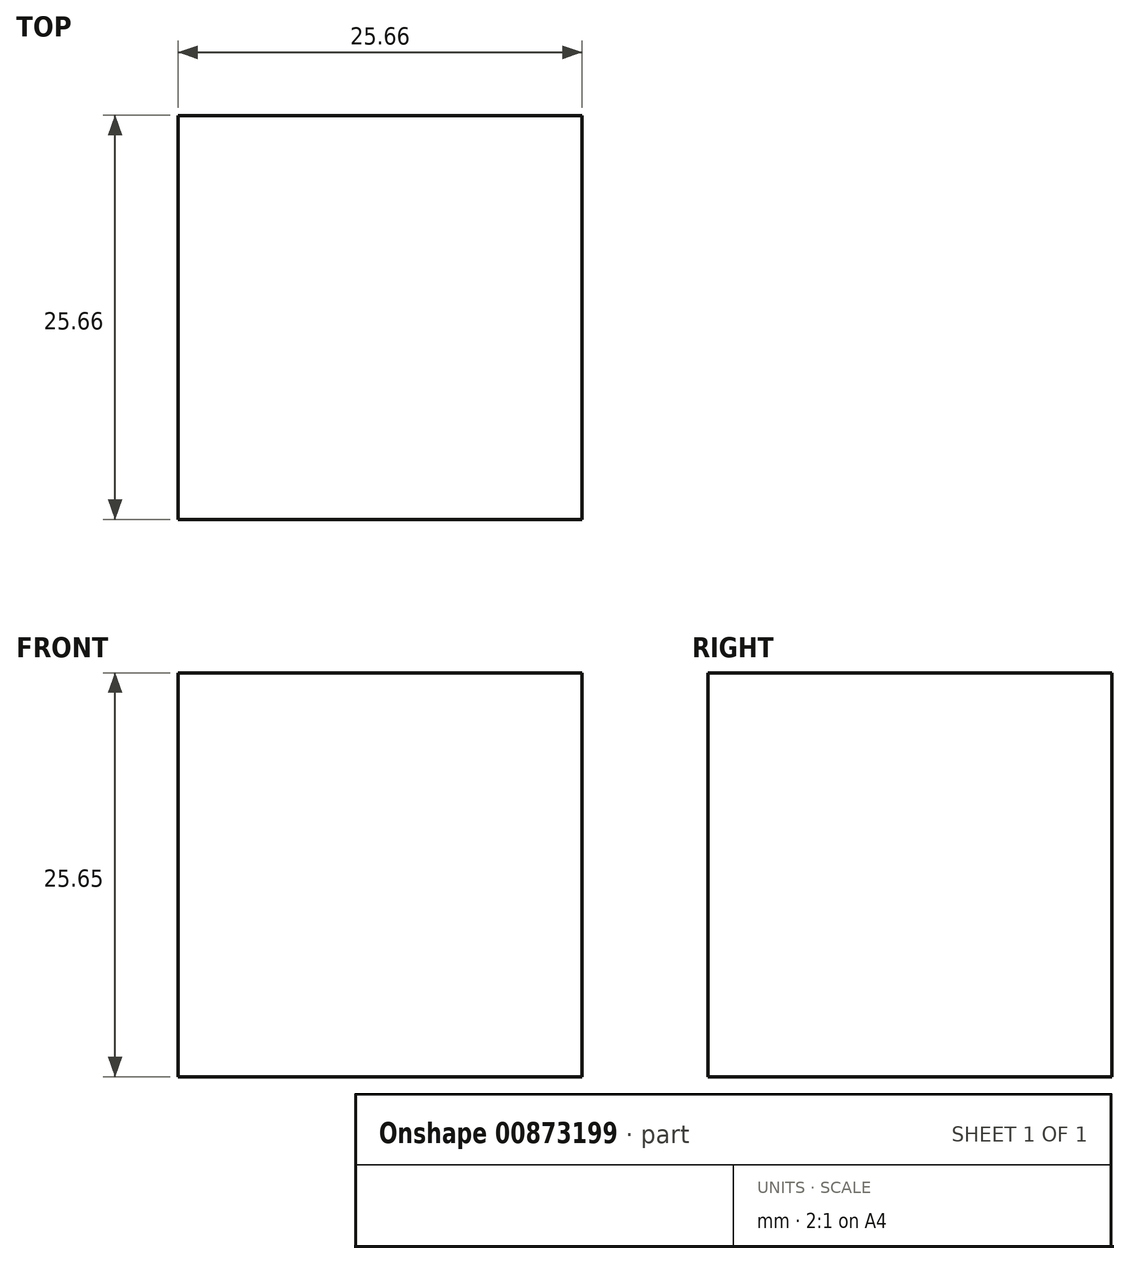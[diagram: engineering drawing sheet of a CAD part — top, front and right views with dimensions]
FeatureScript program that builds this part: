
annotation { "Feature Type Name" : "Feature", "Feature Type Description" : "" }
export const myFeature = defineFeature(function(context is Context, id is Id, definition is map)
    precondition{}
    {
        {
            var Q0;
            Q0=qCreatedBy(makeId("Front.planeOp"),FACE);
            var sketch = newSketch(context, id + "F0", { "sketchPlane" : qUnion([Q0])});
            skLineSegment(sketch, "E0.bottom", {"start": v(-20.2, 0) * mm, "end": v(5.45, 0) * mm});
            skLineSegment(sketch, "E0.top", {"start": v(-20.2, -25.65) * mm, "end": v(5.45, -25.65) * mm});
            skLineSegment(sketch, "E0.left", {"start": v(-20.2, 0) * mm, "end": v(-20.2, -25.65) * mm});
            skLineSegment(sketch, "E0.right", {"start": v(5.45, 0) * mm, "end": v(5.45, -25.65) * mm});
            skSolve(sketch);
        }
        {
            var Q0;
            Q0=makeQuery(id+"F0.imprint","IMPRINT",FACE,{"disambiguationData":[TD([[makeQuery(id+"F0.imprint","IMPRINT",EDGE,{"derivedFrom":sQuery(id+"F0.wireOp",EDGE,"E0.bottom")}),-1.0]])]});
            extrude(context, id + "F1", {"entities" : qUnion([Q0]), "endBound" : BoundingType.SYMMETRIC, "depth" : 25.65 * mm, "offsetDistance" : 25.4 * mm});
        }
    });
